# Revit family: Furniture-Counter_Top-KALLISTA-One-P46009
name_source: partatom
category: Specialty Equipment
units: mm (PartAtom-declared; Revit-internal decimal feet)

## family parameters
Cut with Voids When Loaded = No
Host = Face
Maintain Annotation Orientation = No
OmniClass Number = 23.21.19.15
OmniClass Title = Specialty Casework
Part Type = Normal
Room Calculation Point = No
Round Connector Dimension = Use Diameter
Shared = No

## types (2) — shared parameters
ADA Compliant = No
Assembly Code = E20
Date Modified = 05/20/2025
Default Elevation = 48"
Description = Console Table Top
Height = 1 3/16"
Length = 21 5/16"
Manufacturer = Kallista  Co.
Master Format 2014 = 06 41 93
Master Format 2014 Name = Cabinet and Drawer Hardware
Material = Premium Metal Construction
Product Documentation Link = https://techcomm.kohler.com
Product Name = One
Product Page URL = https://www.kallista.com
URL = https://www.kallista.com
WaterSense Certified = No
Width = 24 3/16"

## per-type parameters (varying)
| type | Finish | Model | Type |
| NM-Nero Marouina | Kallista-Stone-NM-Nero_Marouina | P46009-00-NM | 1 |
| WC-White Carrara | Kallista-Stone-WC-White_Carrara | P46009-00-WC | 2 |

## geometry (parser evidence)
native form markers: Sweep x5
no freeform markers — native parametric forms only
